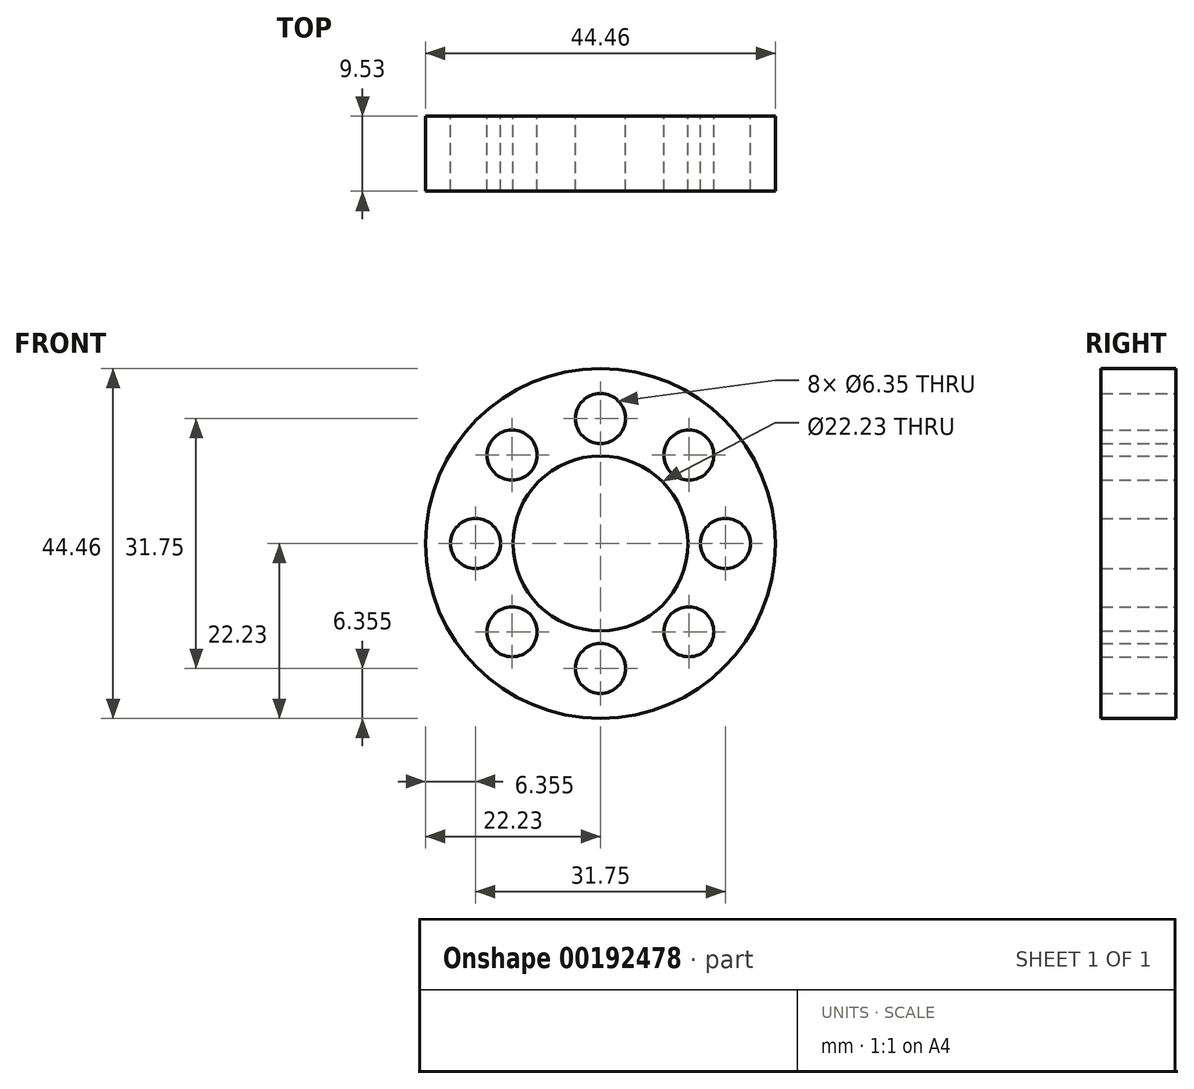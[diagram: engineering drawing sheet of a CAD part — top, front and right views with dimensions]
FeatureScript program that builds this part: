
annotation { "Feature Type Name" : "Feature", "Feature Type Description" : "" }
export const myFeature = defineFeature(function(context is Context, id is Id, definition is map)
    precondition{}
    {
        {
            var Q0;
            Q0=qCreatedBy(makeId("Front.planeOp"),FACE);
            var sketch = newSketch(context, id + "F0", { "sketchPlane" : qUnion([Q0])});
            skCircle(sketch, "E0", {"center": v(0, 0) * mm, "radius": 22.23 * mm});
            skCircle(sketch, "E1", {"center": v(0, 0) * mm, "radius": 11.11 * mm});
            skCircle(sketch, "E2", {"center": v(0, 0) * mm, "radius": 15.88 * mm});
            skCircle(sketch, "E3", {"center": v(0, 15.88) * mm, "radius": 3.18 * mm});
            skCircle(sketch, "E4.1.0", {"center": v(-11.23, 11.23) * mm, "radius": 3.18 * mm});
            skCircle(sketch, "E4.2.0", {"center": v(-15.88, 0) * mm, "radius": 3.18 * mm});
            skCircle(sketch, "E4.3.0", {"center": v(-11.23, -11.23) * mm, "radius": 3.18 * mm});
            skCircle(sketch, "E4.4.0", {"center": v(0, -15.88) * mm, "radius": 3.18 * mm});
            skCircle(sketch, "E4.5.0", {"center": v(11.23, -11.23) * mm, "radius": 3.18 * mm});
            skCircle(sketch, "E4.6.0", {"center": v(15.88, 0) * mm, "radius": 3.18 * mm});
            skCircle(sketch, "E4.7.0", {"center": v(11.23, 11.23) * mm, "radius": 3.18 * mm});
            skSolve(sketch);
        }
        {
            var Q0;
            Q0 = qSketchRegion(id + "F0", true);
            var Q1;
            Q1=makeQuery(id+"F0.imprint","IMPRINT",FACE,{"disambiguationData":[TD([[makeQuery(id+"F0.imprint","IMPRINT",EDGE,{"derivedFrom":sQuery(id+"F0.wireOp",EDGE,"E1")}),-1.0]])]});
            extrude(context, id + "F1", {"entities" : qUnion([Q0, Q1]), "depth" : 9.52 * mm});
        }
    });
